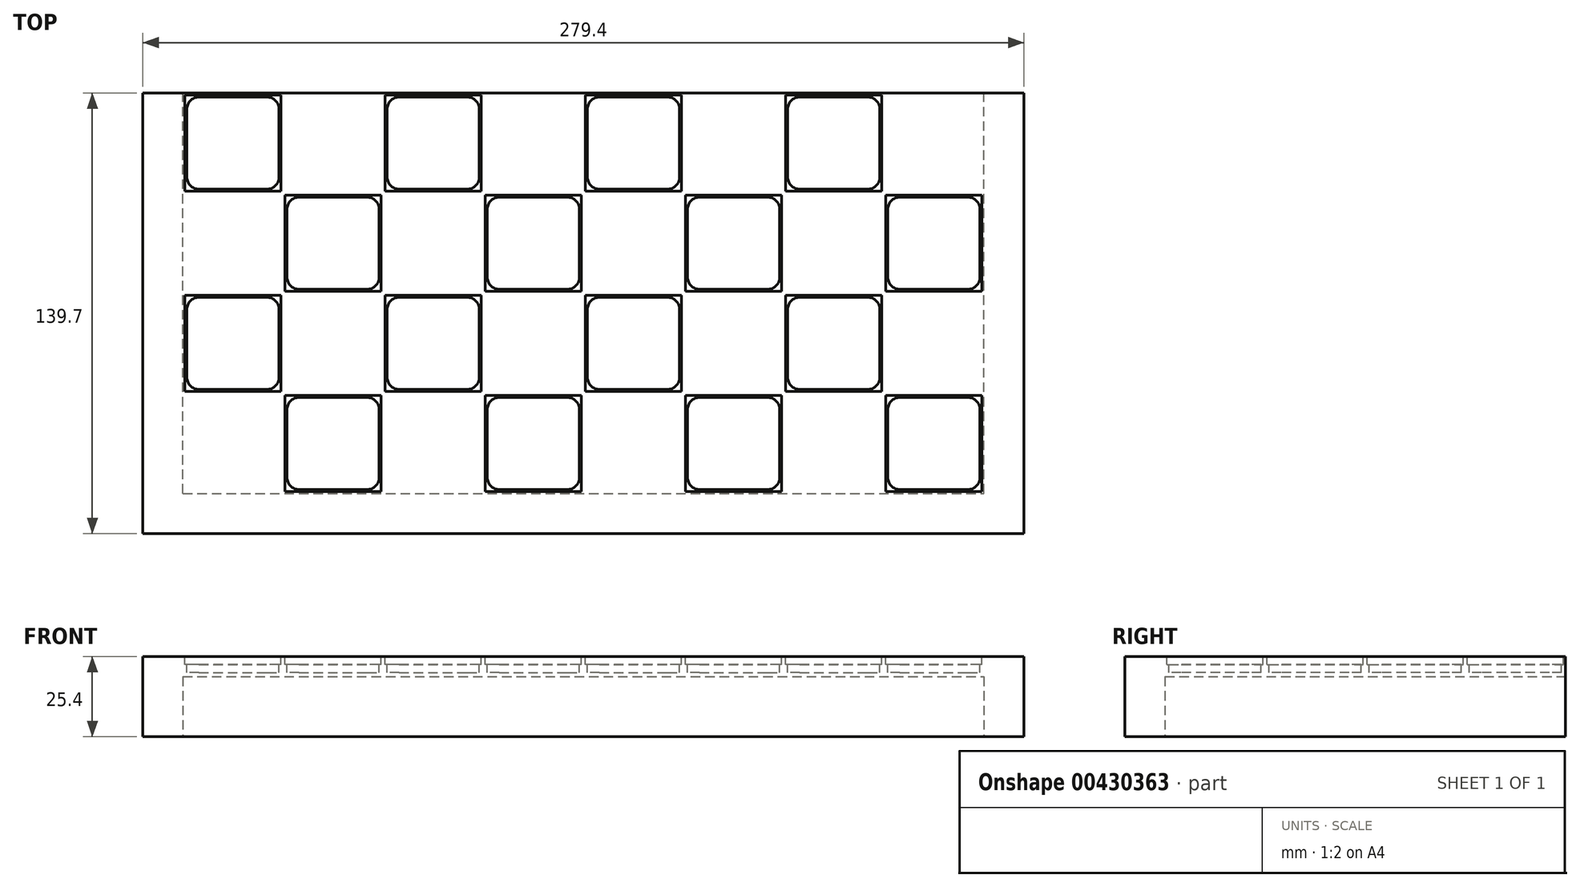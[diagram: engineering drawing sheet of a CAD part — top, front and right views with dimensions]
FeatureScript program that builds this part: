
annotation { "Feature Type Name" : "Feature", "Feature Type Description" : "" }
export const myFeature = defineFeature(function(context is Context, id is Id, definition is map)
    precondition{}
    {
        {
            var Q0;
            Q0=qCreatedBy(makeId("Front.planeOp"),FACE);
            var sketch = newSketch(context, id + "F0", { "sketchPlane" : qUnion([Q0])});
            skLineSegment(sketch, "E0.bottom", {"start": v(-139.7, 12.7) * mm, "end": v(139.7, 12.7) * mm});
            skLineSegment(sketch, "E0.top", {"start": v(-139.7, -12.7) * mm, "end": v(139.7, -12.7) * mm});
            skLineSegment(sketch, "E0.left", {"start": v(-139.7, 12.7) * mm, "end": v(-139.7, -12.7) * mm});
            skLineSegment(sketch, "E0.right", {"start": v(139.7, 12.7) * mm, "end": v(139.7, -12.7) * mm});
            skPoint(sketch, "E0.middle", {"position": v(0, 0) * mm});
            skSolve(sketch);
        }
        {
            var Q0;
            Q0 = qSketchRegion(id + "F0", true);
            extrude(context, id + "F1", {"entities" : qUnion([Q0]), "depth" : 139.7 * mm});
        }
        {
            var Q0;
            Q0=makeQuery(id+"F1.opExtrude","SWEPT_FACE",FACE,{"disambiguationData":[OSD([sQuery(id+"F0.wireOp",EDGE,"E0.bottom")])]});
            var sketch = newSketch(context, id + "F2", { "sketchPlane" : qUnion([Q0])});
            skLineSegment(sketch, "E1", {"start": v(0, 0) * mm, "end": v(0, -127) * mm, "construction": true});
            skPoint(sketch, "E2", {"position": v(-127, 0) * mm});
            skPoint(sketch, "E3", {"position": v(127, 0) * mm});
            skLineSegment(sketch, "E4", {"start": v(-127, 0) * mm, "end": v(-127, -127) * mm, "construction": true});
            skLineSegment(sketch, "E5", {"start": v(127, 0) * mm, "end": v(127, -127) * mm, "construction": true});
            skLineSegment(sketch, "E6", {"start": v(-127, -31.75) * mm, "end": v(127, -31.75) * mm, "construction": true});
            skLineSegment(sketch, "E7", {"start": v(-127, -63.5) * mm, "end": v(127, -63.5) * mm, "construction": true});
            skLineSegment(sketch, "E8", {"start": v(-127, -95.25) * mm, "end": v(127, -95.25) * mm, "construction": true});
            skLineSegment(sketch, "E9", {"start": v(-127, -127) * mm, "end": v(127, -127) * mm, "construction": true});
            skLineSegment(sketch, "E10.1.0.0", {"start": v(-95.25, 0) * mm, "end": v(-95.25, -127) * mm, "construction": true});
            skLineSegment(sketch, "E10.2.0.0", {"start": v(-63.5, 0) * mm, "end": v(-63.5, -127) * mm, "construction": true});
            skLineSegment(sketch, "E10.3.0.0", {"start": v(-31.75, 0) * mm, "end": v(-31.75, -127) * mm, "construction": true});
            skLineSegment(sketch, "E10.4.0.0", {"start": v(0, 0) * mm, "end": v(0, -139.7) * mm, "construction": true});
            skLineSegment(sketch, "E10.5.0.0", {"start": v(31.75, 0) * mm, "end": v(31.75, -127) * mm, "construction": true});
            skLineSegment(sketch, "E10.6.0.0", {"start": v(63.5, 0) * mm, "end": v(63.5, -127) * mm, "construction": true});
            skLineSegment(sketch, "E10.7.0.0", {"start": v(95.25, 0) * mm, "end": v(95.25, -127) * mm, "construction": true});
            skLineSegment(sketch, "E10.direction1", {"start": v(-127, -139.7) * mm, "end": v(-95.25, -139.7) * mm, "construction": true});
            skPoint(sketch, "E11.orphan", {"position": v(-63.5, -139.7) * mm});
            skPoint(sketch, "E12.orphan", {"position": v(-31.75, -139.7) * mm});
            skPoint(sketch, "E13.orphan", {"position": v(0, -139.7) * mm});
            skPoint(sketch, "E14.orphan", {"position": v(31.75, -139.7) * mm});
            skPoint(sketch, "E15.orphan", {"position": v(63.5, -139.7) * mm});
            skPoint(sketch, "E16.orphan", {"position": v(95.25, -139.7) * mm});
            skLineSegment(sketch, "E17", {"start": v(-127, -31.75) * mm, "end": v(-95.25, 0) * mm, "construction": true});
            skLineSegment(sketch, "E18", {"start": v(-127, 0) * mm, "end": v(-95.25, -31.75) * mm, "construction": true});
            skPoint(sketch, "E19", {"position": v(-111.12, -15.88) * mm});
            skLineSegment(sketch, "E20.bottom", {"start": v(-121.92, -1.27) * mm, "end": v(-100.33, -1.27) * mm});
            skLineSegment(sketch, "E20.top", {"start": v(-121.92, -30.48) * mm, "end": v(-100.33, -30.48) * mm});
            skLineSegment(sketch, "E20.left", {"start": v(-125.73, -5.08) * mm, "end": v(-125.73, -26.67) * mm});
            skLineSegment(sketch, "E20.right", {"start": v(-96.52, -5.08) * mm, "end": v(-96.52, -26.67) * mm});
            skPoint(sketch, "E21.visualSharp", {"position": v(-125.73, -1.27) * mm});
            skArc(sketch, "E21.filletArc", {"start": v(-121.92, -1.27) * mm, "mid": v(-124.61, -2.39) * mm, "end": v(-125.73, -5.08) * mm});
            skPoint(sketch, "E22.visualSharp", {"position": v(-96.52, -1.27) * mm});
            skArc(sketch, "E22.filletArc", {"start": v(-96.52, -5.08) * mm, "mid": v(-97.64, -2.39) * mm, "end": v(-100.33, -1.27) * mm});
            skPoint(sketch, "E23.visualSharp", {"position": v(-96.52, -30.48) * mm});
            skArc(sketch, "E23.filletArc", {"start": v(-100.33, -30.48) * mm, "mid": v(-97.64, -29.36) * mm, "end": v(-96.52, -26.67) * mm});
            skPoint(sketch, "E24.visualSharp", {"position": v(-125.73, -30.48) * mm});
            skArc(sketch, "E24.filletArc", {"start": v(-125.73, -26.67) * mm, "mid": v(-124.61, -29.36) * mm, "end": v(-121.92, -30.48) * mm});
            skLineSegment(sketch, "E25.0.1.0", {"start": v(-125.73, -36.83) * mm, "end": v(-125.73, -58.42) * mm});
            skArc(sketch, "E25.0.1.1", {"start": v(-121.92, -33.02) * mm, "mid": v(-124.61, -34.14) * mm, "end": v(-125.73, -36.83) * mm});
            skLineSegment(sketch, "E25.0.1.2", {"start": v(-121.92, -33.02) * mm, "end": v(-100.33, -33.02) * mm});
            skArc(sketch, "E25.0.1.3", {"start": v(-96.52, -36.83) * mm, "mid": v(-97.64, -34.14) * mm, "end": v(-100.33, -33.02) * mm});
            skLineSegment(sketch, "E25.0.1.4", {"start": v(-96.52, -36.83) * mm, "end": v(-96.52, -58.42) * mm});
            skArc(sketch, "E25.0.1.5", {"start": v(-100.33, -62.23) * mm, "mid": v(-97.64, -61.11) * mm, "end": v(-96.52, -58.42) * mm});
            skLineSegment(sketch, "E25.0.1.6", {"start": v(-121.92, -62.23) * mm, "end": v(-100.33, -62.23) * mm});
            skArc(sketch, "E25.0.1.7", {"start": v(-125.73, -58.42) * mm, "mid": v(-124.61, -61.11) * mm, "end": v(-121.92, -62.23) * mm});
            skLineSegment(sketch, "E25.0.2.0", {"start": v(-125.73, -68.58) * mm, "end": v(-125.73, -90.17) * mm});
            skArc(sketch, "E25.0.2.1", {"start": v(-121.92, -64.77) * mm, "mid": v(-124.61, -65.89) * mm, "end": v(-125.73, -68.58) * mm});
            skLineSegment(sketch, "E25.0.2.2", {"start": v(-121.92, -64.77) * mm, "end": v(-100.33, -64.77) * mm});
            skArc(sketch, "E25.0.2.3", {"start": v(-96.52, -68.58) * mm, "mid": v(-97.64, -65.89) * mm, "end": v(-100.33, -64.77) * mm});
            skLineSegment(sketch, "E25.0.2.4", {"start": v(-96.52, -68.58) * mm, "end": v(-96.52, -90.17) * mm});
            skArc(sketch, "E25.0.2.5", {"start": v(-100.33, -93.98) * mm, "mid": v(-97.64, -92.86) * mm, "end": v(-96.52, -90.17) * mm});
            skLineSegment(sketch, "E25.0.2.6", {"start": v(-121.92, -93.98) * mm, "end": v(-100.33, -93.98) * mm});
            skArc(sketch, "E25.0.2.7", {"start": v(-125.73, -90.17) * mm, "mid": v(-124.61, -92.86) * mm, "end": v(-121.92, -93.98) * mm});
            skLineSegment(sketch, "E25.0.3.0", {"start": v(-125.73, -100.33) * mm, "end": v(-125.73, -121.92) * mm});
            skArc(sketch, "E25.0.3.1", {"start": v(-121.92, -96.52) * mm, "mid": v(-124.61, -97.64) * mm, "end": v(-125.73, -100.33) * mm});
            skLineSegment(sketch, "E25.0.3.2", {"start": v(-121.92, -96.52) * mm, "end": v(-100.33, -96.52) * mm});
            skArc(sketch, "E25.0.3.3", {"start": v(-96.52, -100.33) * mm, "mid": v(-97.64, -97.64) * mm, "end": v(-100.33, -96.52) * mm});
            skLineSegment(sketch, "E25.0.3.4", {"start": v(-96.52, -100.33) * mm, "end": v(-96.52, -121.92) * mm});
            skArc(sketch, "E25.0.3.5", {"start": v(-100.33, -125.73) * mm, "mid": v(-97.64, -124.61) * mm, "end": v(-96.52, -121.92) * mm});
            skLineSegment(sketch, "E25.0.3.6", {"start": v(-121.92, -125.73) * mm, "end": v(-100.33, -125.73) * mm});
            skArc(sketch, "E25.0.3.7", {"start": v(-125.73, -121.92) * mm, "mid": v(-124.61, -124.61) * mm, "end": v(-121.92, -125.73) * mm});
            skLineSegment(sketch, "E25.1.0.0", {"start": v(-93.98, -5.08) * mm, "end": v(-93.98, -26.67) * mm});
            skArc(sketch, "E25.1.0.1", {"start": v(-90.17, -1.27) * mm, "mid": v(-92.86, -2.39) * mm, "end": v(-93.98, -5.08) * mm});
            skLineSegment(sketch, "E25.1.0.2", {"start": v(-90.17, -1.27) * mm, "end": v(-68.58, -1.27) * mm});
            skArc(sketch, "E25.1.0.3", {"start": v(-64.77, -5.08) * mm, "mid": v(-65.89, -2.39) * mm, "end": v(-68.58, -1.27) * mm});
            skLineSegment(sketch, "E25.1.0.4", {"start": v(-64.77, -5.08) * mm, "end": v(-64.77, -26.67) * mm});
            skArc(sketch, "E25.1.0.5", {"start": v(-68.58, -30.48) * mm, "mid": v(-65.89, -29.36) * mm, "end": v(-64.77, -26.67) * mm});
            skLineSegment(sketch, "E25.1.0.6", {"start": v(-90.17, -30.48) * mm, "end": v(-68.58, -30.48) * mm});
            skArc(sketch, "E25.1.0.7", {"start": v(-93.98, -26.67) * mm, "mid": v(-92.86, -29.36) * mm, "end": v(-90.17, -30.48) * mm});
            skLineSegment(sketch, "E25.1.1.0", {"start": v(-93.98, -36.83) * mm, "end": v(-93.98, -58.42) * mm});
            skArc(sketch, "E25.1.1.1", {"start": v(-90.17, -33.02) * mm, "mid": v(-92.86, -34.14) * mm, "end": v(-93.98, -36.83) * mm});
            skLineSegment(sketch, "E25.1.1.2", {"start": v(-90.17, -33.02) * mm, "end": v(-68.58, -33.02) * mm});
            skArc(sketch, "E25.1.1.3", {"start": v(-64.77, -36.83) * mm, "mid": v(-65.89, -34.14) * mm, "end": v(-68.58, -33.02) * mm});
            skLineSegment(sketch, "E25.1.1.4", {"start": v(-64.77, -36.83) * mm, "end": v(-64.77, -58.42) * mm});
            skArc(sketch, "E25.1.1.5", {"start": v(-68.58, -62.23) * mm, "mid": v(-65.89, -61.11) * mm, "end": v(-64.77, -58.42) * mm});
            skLineSegment(sketch, "E25.1.1.6", {"start": v(-90.17, -62.23) * mm, "end": v(-68.58, -62.23) * mm});
            skArc(sketch, "E25.1.1.7", {"start": v(-93.98, -58.42) * mm, "mid": v(-92.86, -61.11) * mm, "end": v(-90.17, -62.23) * mm});
            skLineSegment(sketch, "E25.1.2.0", {"start": v(-93.98, -68.58) * mm, "end": v(-93.98, -90.17) * mm});
            skArc(sketch, "E25.1.2.1", {"start": v(-90.17, -64.77) * mm, "mid": v(-92.86, -65.89) * mm, "end": v(-93.98, -68.58) * mm});
            skLineSegment(sketch, "E25.1.2.2", {"start": v(-90.17, -64.77) * mm, "end": v(-68.58, -64.77) * mm});
            skArc(sketch, "E25.1.2.3", {"start": v(-64.77, -68.58) * mm, "mid": v(-65.89, -65.89) * mm, "end": v(-68.58, -64.77) * mm});
            skLineSegment(sketch, "E25.1.2.4", {"start": v(-64.77, -68.58) * mm, "end": v(-64.77, -90.17) * mm});
            skArc(sketch, "E25.1.2.5", {"start": v(-68.58, -93.98) * mm, "mid": v(-65.89, -92.86) * mm, "end": v(-64.77, -90.17) * mm});
            skLineSegment(sketch, "E25.1.2.6", {"start": v(-90.17, -93.98) * mm, "end": v(-68.58, -93.98) * mm});
            skArc(sketch, "E25.1.2.7", {"start": v(-93.98, -90.17) * mm, "mid": v(-92.86, -92.86) * mm, "end": v(-90.17, -93.98) * mm});
            skLineSegment(sketch, "E25.1.3.0", {"start": v(-93.98, -100.33) * mm, "end": v(-93.98, -121.92) * mm});
            skArc(sketch, "E25.1.3.1", {"start": v(-90.17, -96.52) * mm, "mid": v(-92.86, -97.64) * mm, "end": v(-93.98, -100.33) * mm});
            skLineSegment(sketch, "E25.1.3.2", {"start": v(-90.17, -96.52) * mm, "end": v(-68.58, -96.52) * mm});
            skArc(sketch, "E25.1.3.3", {"start": v(-64.77, -100.33) * mm, "mid": v(-65.89, -97.64) * mm, "end": v(-68.58, -96.52) * mm});
            skLineSegment(sketch, "E25.1.3.4", {"start": v(-64.77, -100.33) * mm, "end": v(-64.77, -121.92) * mm});
            skArc(sketch, "E25.1.3.5", {"start": v(-68.58, -125.73) * mm, "mid": v(-65.89, -124.61) * mm, "end": v(-64.77, -121.92) * mm});
            skLineSegment(sketch, "E25.1.3.6", {"start": v(-90.17, -125.73) * mm, "end": v(-68.58, -125.73) * mm});
            skArc(sketch, "E25.1.3.7", {"start": v(-93.98, -121.92) * mm, "mid": v(-92.86, -124.61) * mm, "end": v(-90.17, -125.73) * mm});
            skLineSegment(sketch, "E25.2.0.0", {"start": v(-62.23, -5.08) * mm, "end": v(-62.23, -26.67) * mm});
            skArc(sketch, "E25.2.0.1", {"start": v(-58.42, -1.27) * mm, "mid": v(-61.11, -2.39) * mm, "end": v(-62.23, -5.08) * mm});
            skLineSegment(sketch, "E25.2.0.2", {"start": v(-58.42, -1.27) * mm, "end": v(-36.83, -1.27) * mm});
            skArc(sketch, "E25.2.0.3", {"start": v(-33.02, -5.08) * mm, "mid": v(-34.14, -2.39) * mm, "end": v(-36.83, -1.27) * mm});
            skLineSegment(sketch, "E25.2.0.4", {"start": v(-33.02, -5.08) * mm, "end": v(-33.02, -26.67) * mm});
            skArc(sketch, "E25.2.0.5", {"start": v(-36.83, -30.48) * mm, "mid": v(-34.14, -29.36) * mm, "end": v(-33.02, -26.67) * mm});
            skLineSegment(sketch, "E25.2.0.6", {"start": v(-58.42, -30.48) * mm, "end": v(-36.83, -30.48) * mm});
            skArc(sketch, "E25.2.0.7", {"start": v(-62.23, -26.67) * mm, "mid": v(-61.11, -29.36) * mm, "end": v(-58.42, -30.48) * mm});
            skLineSegment(sketch, "E25.2.1.0", {"start": v(-62.23, -36.83) * mm, "end": v(-62.23, -58.42) * mm});
            skArc(sketch, "E25.2.1.1", {"start": v(-58.42, -33.02) * mm, "mid": v(-61.11, -34.14) * mm, "end": v(-62.23, -36.83) * mm});
            skLineSegment(sketch, "E25.2.1.2", {"start": v(-58.42, -33.02) * mm, "end": v(-36.83, -33.02) * mm});
            skArc(sketch, "E25.2.1.3", {"start": v(-33.02, -36.83) * mm, "mid": v(-34.14, -34.14) * mm, "end": v(-36.83, -33.02) * mm});
            skLineSegment(sketch, "E25.2.1.4", {"start": v(-33.02, -36.83) * mm, "end": v(-33.02, -58.42) * mm});
            skArc(sketch, "E25.2.1.5", {"start": v(-36.83, -62.23) * mm, "mid": v(-34.14, -61.11) * mm, "end": v(-33.02, -58.42) * mm});
            skLineSegment(sketch, "E25.2.1.6", {"start": v(-58.42, -62.23) * mm, "end": v(-36.83, -62.23) * mm});
            skArc(sketch, "E25.2.1.7", {"start": v(-62.23, -58.42) * mm, "mid": v(-61.11, -61.11) * mm, "end": v(-58.42, -62.23) * mm});
            skLineSegment(sketch, "E25.2.2.0", {"start": v(-62.23, -68.58) * mm, "end": v(-62.23, -90.17) * mm});
            skArc(sketch, "E25.2.2.1", {"start": v(-58.42, -64.77) * mm, "mid": v(-61.11, -65.89) * mm, "end": v(-62.23, -68.58) * mm});
            skLineSegment(sketch, "E25.2.2.2", {"start": v(-58.42, -64.77) * mm, "end": v(-36.83, -64.77) * mm});
            skArc(sketch, "E25.2.2.3", {"start": v(-33.02, -68.58) * mm, "mid": v(-34.14, -65.89) * mm, "end": v(-36.83, -64.77) * mm});
            skLineSegment(sketch, "E25.2.2.4", {"start": v(-33.02, -68.58) * mm, "end": v(-33.02, -90.17) * mm});
            skArc(sketch, "E25.2.2.5", {"start": v(-36.83, -93.98) * mm, "mid": v(-34.14, -92.86) * mm, "end": v(-33.02, -90.17) * mm});
            skLineSegment(sketch, "E25.2.2.6", {"start": v(-58.42, -93.98) * mm, "end": v(-36.83, -93.98) * mm});
            skArc(sketch, "E25.2.2.7", {"start": v(-62.23, -90.17) * mm, "mid": v(-61.11, -92.86) * mm, "end": v(-58.42, -93.98) * mm});
            skLineSegment(sketch, "E25.2.3.0", {"start": v(-62.23, -100.33) * mm, "end": v(-62.23, -121.92) * mm});
            skArc(sketch, "E25.2.3.1", {"start": v(-58.42, -96.52) * mm, "mid": v(-61.11, -97.64) * mm, "end": v(-62.23, -100.33) * mm});
            skLineSegment(sketch, "E25.2.3.2", {"start": v(-58.42, -96.52) * mm, "end": v(-36.83, -96.52) * mm});
            skArc(sketch, "E25.2.3.3", {"start": v(-33.02, -100.33) * mm, "mid": v(-34.14, -97.64) * mm, "end": v(-36.83, -96.52) * mm});
            skLineSegment(sketch, "E25.2.3.4", {"start": v(-33.02, -100.33) * mm, "end": v(-33.02, -121.92) * mm});
            skArc(sketch, "E25.2.3.5", {"start": v(-36.83, -125.73) * mm, "mid": v(-34.14, -124.61) * mm, "end": v(-33.02, -121.92) * mm});
            skLineSegment(sketch, "E25.2.3.6", {"start": v(-58.42, -125.73) * mm, "end": v(-36.83, -125.73) * mm});
            skArc(sketch, "E25.2.3.7", {"start": v(-62.23, -121.92) * mm, "mid": v(-61.11, -124.61) * mm, "end": v(-58.42, -125.73) * mm});
            skLineSegment(sketch, "E25.3.0.0", {"start": v(-30.48, -5.08) * mm, "end": v(-30.48, -26.67) * mm});
            skArc(sketch, "E25.3.0.1", {"start": v(-26.67, -1.27) * mm, "mid": v(-29.36, -2.39) * mm, "end": v(-30.48, -5.08) * mm});
            skLineSegment(sketch, "E25.3.0.2", {"start": v(-26.67, -1.27) * mm, "end": v(-5.08, -1.27) * mm});
            skArc(sketch, "E25.3.0.3", {"start": v(-1.27, -5.08) * mm, "mid": v(-2.39, -2.39) * mm, "end": v(-5.08, -1.27) * mm});
            skLineSegment(sketch, "E25.3.0.4", {"start": v(-1.27, -5.08) * mm, "end": v(-1.27, -26.67) * mm});
            skArc(sketch, "E25.3.0.5", {"start": v(-5.08, -30.48) * mm, "mid": v(-2.39, -29.36) * mm, "end": v(-1.27, -26.67) * mm});
            skLineSegment(sketch, "E25.3.0.6", {"start": v(-26.67, -30.48) * mm, "end": v(-5.08, -30.48) * mm});
            skArc(sketch, "E25.3.0.7", {"start": v(-30.48, -26.67) * mm, "mid": v(-29.36, -29.36) * mm, "end": v(-26.67, -30.48) * mm});
            skLineSegment(sketch, "E25.3.1.0", {"start": v(-30.48, -36.83) * mm, "end": v(-30.48, -58.42) * mm});
            skArc(sketch, "E25.3.1.1", {"start": v(-26.67, -33.02) * mm, "mid": v(-29.36, -34.14) * mm, "end": v(-30.48, -36.83) * mm});
            skLineSegment(sketch, "E25.3.1.2", {"start": v(-26.67, -33.02) * mm, "end": v(-5.08, -33.02) * mm});
            skArc(sketch, "E25.3.1.3", {"start": v(-1.27, -36.83) * mm, "mid": v(-2.39, -34.14) * mm, "end": v(-5.08, -33.02) * mm});
            skLineSegment(sketch, "E25.3.1.4", {"start": v(-1.27, -36.83) * mm, "end": v(-1.27, -58.42) * mm});
            skArc(sketch, "E25.3.1.5", {"start": v(-5.08, -62.23) * mm, "mid": v(-2.39, -61.11) * mm, "end": v(-1.27, -58.42) * mm});
            skLineSegment(sketch, "E25.3.1.6", {"start": v(-26.67, -62.23) * mm, "end": v(-5.08, -62.23) * mm});
            skArc(sketch, "E25.3.1.7", {"start": v(-30.48, -58.42) * mm, "mid": v(-29.36, -61.11) * mm, "end": v(-26.67, -62.23) * mm});
            skLineSegment(sketch, "E25.3.2.0", {"start": v(-30.48, -68.58) * mm, "end": v(-30.48, -90.17) * mm});
            skArc(sketch, "E25.3.2.1", {"start": v(-26.67, -64.77) * mm, "mid": v(-29.36, -65.89) * mm, "end": v(-30.48, -68.58) * mm});
            skLineSegment(sketch, "E25.3.2.2", {"start": v(-26.67, -64.77) * mm, "end": v(-5.08, -64.77) * mm});
            skArc(sketch, "E25.3.2.3", {"start": v(-1.27, -68.58) * mm, "mid": v(-2.39, -65.89) * mm, "end": v(-5.08, -64.77) * mm});
            skLineSegment(sketch, "E25.3.2.4", {"start": v(-1.27, -68.58) * mm, "end": v(-1.27, -90.17) * mm});
            skArc(sketch, "E25.3.2.5", {"start": v(-5.08, -93.98) * mm, "mid": v(-2.39, -92.86) * mm, "end": v(-1.27, -90.17) * mm});
            skLineSegment(sketch, "E25.3.2.6", {"start": v(-26.67, -93.98) * mm, "end": v(-5.08, -93.98) * mm});
            skArc(sketch, "E25.3.2.7", {"start": v(-30.48, -90.17) * mm, "mid": v(-29.36, -92.86) * mm, "end": v(-26.67, -93.98) * mm});
            skLineSegment(sketch, "E25.3.3.0", {"start": v(-30.48, -100.33) * mm, "end": v(-30.48, -121.92) * mm});
            skArc(sketch, "E25.3.3.1", {"start": v(-26.67, -96.52) * mm, "mid": v(-29.36, -97.64) * mm, "end": v(-30.48, -100.33) * mm});
            skLineSegment(sketch, "E25.3.3.2", {"start": v(-26.67, -96.52) * mm, "end": v(-5.08, -96.52) * mm});
            skArc(sketch, "E25.3.3.3", {"start": v(-1.27, -100.33) * mm, "mid": v(-2.39, -97.64) * mm, "end": v(-5.08, -96.52) * mm});
            skLineSegment(sketch, "E25.3.3.4", {"start": v(-1.27, -100.33) * mm, "end": v(-1.27, -121.92) * mm});
            skArc(sketch, "E25.3.3.5", {"start": v(-5.08, -125.73) * mm, "mid": v(-2.39, -124.61) * mm, "end": v(-1.27, -121.92) * mm});
            skLineSegment(sketch, "E25.3.3.6", {"start": v(-26.67, -125.73) * mm, "end": v(-5.08, -125.73) * mm});
            skArc(sketch, "E25.3.3.7", {"start": v(-30.48, -121.92) * mm, "mid": v(-29.36, -124.61) * mm, "end": v(-26.67, -125.73) * mm});
            skLineSegment(sketch, "E25.4.0.0", {"start": v(1.27, -5.08) * mm, "end": v(1.27, -26.67) * mm});
            skArc(sketch, "E25.4.0.1", {"start": v(5.08, -1.27) * mm, "mid": v(2.39, -2.39) * mm, "end": v(1.27, -5.08) * mm});
            skLineSegment(sketch, "E25.4.0.2", {"start": v(5.08, -1.27) * mm, "end": v(26.67, -1.27) * mm});
            skArc(sketch, "E25.4.0.3", {"start": v(30.48, -5.08) * mm, "mid": v(29.36, -2.39) * mm, "end": v(26.67, -1.27) * mm});
            skLineSegment(sketch, "E25.4.0.4", {"start": v(30.48, -5.08) * mm, "end": v(30.48, -26.67) * mm});
            skArc(sketch, "E25.4.0.5", {"start": v(26.67, -30.48) * mm, "mid": v(29.36, -29.36) * mm, "end": v(30.48, -26.67) * mm});
            skLineSegment(sketch, "E25.4.0.6", {"start": v(5.08, -30.48) * mm, "end": v(26.67, -30.48) * mm});
            skArc(sketch, "E25.4.0.7", {"start": v(1.27, -26.67) * mm, "mid": v(2.39, -29.36) * mm, "end": v(5.08, -30.48) * mm});
            skLineSegment(sketch, "E25.4.1.0", {"start": v(1.27, -36.83) * mm, "end": v(1.27, -58.42) * mm});
            skArc(sketch, "E25.4.1.1", {"start": v(5.08, -33.02) * mm, "mid": v(2.39, -34.14) * mm, "end": v(1.27, -36.83) * mm});
            skLineSegment(sketch, "E25.4.1.2", {"start": v(5.08, -33.02) * mm, "end": v(26.67, -33.02) * mm});
            skArc(sketch, "E25.4.1.3", {"start": v(30.48, -36.83) * mm, "mid": v(29.36, -34.14) * mm, "end": v(26.67, -33.02) * mm});
            skLineSegment(sketch, "E25.4.1.4", {"start": v(30.48, -36.83) * mm, "end": v(30.48, -58.42) * mm});
            skArc(sketch, "E25.4.1.5", {"start": v(26.67, -62.23) * mm, "mid": v(29.36, -61.11) * mm, "end": v(30.48, -58.42) * mm});
            skLineSegment(sketch, "E25.4.1.6", {"start": v(5.08, -62.23) * mm, "end": v(26.67, -62.23) * mm});
            skArc(sketch, "E25.4.1.7", {"start": v(1.27, -58.42) * mm, "mid": v(2.39, -61.11) * mm, "end": v(5.08, -62.23) * mm});
            skLineSegment(sketch, "E25.4.2.0", {"start": v(1.27, -68.58) * mm, "end": v(1.27, -90.17) * mm});
            skArc(sketch, "E25.4.2.1", {"start": v(5.08, -64.77) * mm, "mid": v(2.39, -65.89) * mm, "end": v(1.27, -68.58) * mm});
            skLineSegment(sketch, "E25.4.2.2", {"start": v(5.08, -64.77) * mm, "end": v(26.67, -64.77) * mm});
            skArc(sketch, "E25.4.2.3", {"start": v(30.48, -68.58) * mm, "mid": v(29.36, -65.89) * mm, "end": v(26.67, -64.77) * mm});
            skLineSegment(sketch, "E25.4.2.4", {"start": v(30.48, -68.58) * mm, "end": v(30.48, -90.17) * mm});
            skArc(sketch, "E25.4.2.5", {"start": v(26.67, -93.98) * mm, "mid": v(29.36, -92.86) * mm, "end": v(30.48, -90.17) * mm});
            skLineSegment(sketch, "E25.4.2.6", {"start": v(5.08, -93.98) * mm, "end": v(26.67, -93.98) * mm});
            skArc(sketch, "E25.4.2.7", {"start": v(1.27, -90.17) * mm, "mid": v(2.39, -92.86) * mm, "end": v(5.08, -93.98) * mm});
            skLineSegment(sketch, "E25.4.3.0", {"start": v(1.27, -100.33) * mm, "end": v(1.27, -121.92) * mm});
            skArc(sketch, "E25.4.3.1", {"start": v(5.08, -96.52) * mm, "mid": v(2.39, -97.64) * mm, "end": v(1.27, -100.33) * mm});
            skLineSegment(sketch, "E25.4.3.2", {"start": v(5.08, -96.52) * mm, "end": v(26.67, -96.52) * mm});
            skArc(sketch, "E25.4.3.3", {"start": v(30.48, -100.33) * mm, "mid": v(29.36, -97.64) * mm, "end": v(26.67, -96.52) * mm});
            skLineSegment(sketch, "E25.4.3.4", {"start": v(30.48, -100.33) * mm, "end": v(30.48, -121.92) * mm});
            skArc(sketch, "E25.4.3.5", {"start": v(26.67, -125.73) * mm, "mid": v(29.36, -124.61) * mm, "end": v(30.48, -121.92) * mm});
            skLineSegment(sketch, "E25.4.3.6", {"start": v(5.08, -125.73) * mm, "end": v(26.67, -125.73) * mm});
            skArc(sketch, "E25.4.3.7", {"start": v(1.27, -121.92) * mm, "mid": v(2.39, -124.61) * mm, "end": v(5.08, -125.73) * mm});
            skLineSegment(sketch, "E25.5.0.0", {"start": v(33.02, -5.08) * mm, "end": v(33.02, -26.67) * mm});
            skArc(sketch, "E25.5.0.1", {"start": v(36.83, -1.27) * mm, "mid": v(34.14, -2.39) * mm, "end": v(33.02, -5.08) * mm});
            skLineSegment(sketch, "E25.5.0.2", {"start": v(36.83, -1.27) * mm, "end": v(58.42, -1.27) * mm});
            skArc(sketch, "E25.5.0.3", {"start": v(62.23, -5.08) * mm, "mid": v(61.11, -2.39) * mm, "end": v(58.42, -1.27) * mm});
            skLineSegment(sketch, "E25.5.0.4", {"start": v(62.23, -5.08) * mm, "end": v(62.23, -26.67) * mm});
            skArc(sketch, "E25.5.0.5", {"start": v(58.42, -30.48) * mm, "mid": v(61.11, -29.36) * mm, "end": v(62.23, -26.67) * mm});
            skLineSegment(sketch, "E25.5.0.6", {"start": v(36.83, -30.48) * mm, "end": v(58.42, -30.48) * mm});
            skArc(sketch, "E25.5.0.7", {"start": v(33.02, -26.67) * mm, "mid": v(34.14, -29.36) * mm, "end": v(36.83, -30.48) * mm});
            skLineSegment(sketch, "E25.5.1.0", {"start": v(33.02, -36.83) * mm, "end": v(33.02, -58.42) * mm});
            skArc(sketch, "E25.5.1.1", {"start": v(36.83, -33.02) * mm, "mid": v(34.14, -34.14) * mm, "end": v(33.02, -36.83) * mm});
            skLineSegment(sketch, "E25.5.1.2", {"start": v(36.83, -33.02) * mm, "end": v(58.42, -33.02) * mm});
            skArc(sketch, "E25.5.1.3", {"start": v(62.23, -36.83) * mm, "mid": v(61.11, -34.14) * mm, "end": v(58.42, -33.02) * mm});
            skLineSegment(sketch, "E25.5.1.4", {"start": v(62.23, -36.83) * mm, "end": v(62.23, -58.42) * mm});
            skArc(sketch, "E25.5.1.5", {"start": v(58.42, -62.23) * mm, "mid": v(61.11, -61.11) * mm, "end": v(62.23, -58.42) * mm});
            skLineSegment(sketch, "E25.5.1.6", {"start": v(36.83, -62.23) * mm, "end": v(58.42, -62.23) * mm});
            skArc(sketch, "E25.5.1.7", {"start": v(33.02, -58.42) * mm, "mid": v(34.14, -61.11) * mm, "end": v(36.83, -62.23) * mm});
            skLineSegment(sketch, "E25.5.2.0", {"start": v(33.02, -68.58) * mm, "end": v(33.02, -90.17) * mm});
            skArc(sketch, "E25.5.2.1", {"start": v(36.83, -64.77) * mm, "mid": v(34.14, -65.89) * mm, "end": v(33.02, -68.58) * mm});
            skLineSegment(sketch, "E25.5.2.2", {"start": v(36.83, -64.77) * mm, "end": v(58.42, -64.77) * mm});
            skArc(sketch, "E25.5.2.3", {"start": v(62.23, -68.58) * mm, "mid": v(61.11, -65.89) * mm, "end": v(58.42, -64.77) * mm});
            skLineSegment(sketch, "E25.5.2.4", {"start": v(62.23, -68.58) * mm, "end": v(62.23, -90.17) * mm});
            skArc(sketch, "E25.5.2.5", {"start": v(58.42, -93.98) * mm, "mid": v(61.11, -92.86) * mm, "end": v(62.23, -90.17) * mm});
            skLineSegment(sketch, "E25.5.2.6", {"start": v(36.83, -93.98) * mm, "end": v(58.42, -93.98) * mm});
            skArc(sketch, "E25.5.2.7", {"start": v(33.02, -90.17) * mm, "mid": v(34.14, -92.86) * mm, "end": v(36.83, -93.98) * mm});
            skLineSegment(sketch, "E25.5.3.0", {"start": v(33.02, -100.33) * mm, "end": v(33.02, -121.92) * mm});
            skArc(sketch, "E25.5.3.1", {"start": v(36.83, -96.52) * mm, "mid": v(34.14, -97.64) * mm, "end": v(33.02, -100.33) * mm});
            skLineSegment(sketch, "E25.5.3.2", {"start": v(36.83, -96.52) * mm, "end": v(58.42, -96.52) * mm});
            skArc(sketch, "E25.5.3.3", {"start": v(62.23, -100.33) * mm, "mid": v(61.11, -97.64) * mm, "end": v(58.42, -96.52) * mm});
            skLineSegment(sketch, "E25.5.3.4", {"start": v(62.23, -100.33) * mm, "end": v(62.23, -121.92) * mm});
            skArc(sketch, "E25.5.3.5", {"start": v(58.42, -125.73) * mm, "mid": v(61.11, -124.61) * mm, "end": v(62.23, -121.92) * mm});
            skLineSegment(sketch, "E25.5.3.6", {"start": v(36.83, -125.73) * mm, "end": v(58.42, -125.73) * mm});
            skArc(sketch, "E25.5.3.7", {"start": v(33.02, -121.92) * mm, "mid": v(34.14, -124.61) * mm, "end": v(36.83, -125.73) * mm});
            skLineSegment(sketch, "E25.6.0.0", {"start": v(64.77, -5.08) * mm, "end": v(64.77, -26.67) * mm});
            skArc(sketch, "E25.6.0.1", {"start": v(68.58, -1.27) * mm, "mid": v(65.89, -2.39) * mm, "end": v(64.77, -5.08) * mm});
            skLineSegment(sketch, "E25.6.0.2", {"start": v(68.58, -1.27) * mm, "end": v(90.17, -1.27) * mm});
            skArc(sketch, "E25.6.0.3", {"start": v(93.98, -5.08) * mm, "mid": v(92.86, -2.39) * mm, "end": v(90.17, -1.27) * mm});
            skLineSegment(sketch, "E25.6.0.4", {"start": v(93.98, -5.08) * mm, "end": v(93.98, -26.67) * mm});
            skArc(sketch, "E25.6.0.5", {"start": v(90.17, -30.48) * mm, "mid": v(92.86, -29.36) * mm, "end": v(93.98, -26.67) * mm});
            skLineSegment(sketch, "E25.6.0.6", {"start": v(68.58, -30.48) * mm, "end": v(90.17, -30.48) * mm});
            skArc(sketch, "E25.6.0.7", {"start": v(64.77, -26.67) * mm, "mid": v(65.89, -29.36) * mm, "end": v(68.58, -30.48) * mm});
            skLineSegment(sketch, "E25.6.1.0", {"start": v(64.77, -36.83) * mm, "end": v(64.77, -58.42) * mm});
            skArc(sketch, "E25.6.1.1", {"start": v(68.58, -33.02) * mm, "mid": v(65.89, -34.14) * mm, "end": v(64.77, -36.83) * mm});
            skLineSegment(sketch, "E25.6.1.2", {"start": v(68.58, -33.02) * mm, "end": v(90.17, -33.02) * mm});
            skArc(sketch, "E25.6.1.3", {"start": v(93.98, -36.83) * mm, "mid": v(92.86, -34.14) * mm, "end": v(90.17, -33.02) * mm});
            skLineSegment(sketch, "E25.6.1.4", {"start": v(93.98, -36.83) * mm, "end": v(93.98, -58.42) * mm});
            skArc(sketch, "E25.6.1.5", {"start": v(90.17, -62.23) * mm, "mid": v(92.86, -61.11) * mm, "end": v(93.98, -58.42) * mm});
            skLineSegment(sketch, "E25.6.1.6", {"start": v(68.58, -62.23) * mm, "end": v(90.17, -62.23) * mm});
            skArc(sketch, "E25.6.1.7", {"start": v(64.77, -58.42) * mm, "mid": v(65.89, -61.11) * mm, "end": v(68.58, -62.23) * mm});
            skLineSegment(sketch, "E25.6.2.0", {"start": v(64.77, -68.58) * mm, "end": v(64.77, -90.17) * mm});
            skArc(sketch, "E25.6.2.1", {"start": v(68.58, -64.77) * mm, "mid": v(65.89, -65.89) * mm, "end": v(64.77, -68.58) * mm});
            skLineSegment(sketch, "E25.6.2.2", {"start": v(68.58, -64.77) * mm, "end": v(90.17, -64.77) * mm});
            skArc(sketch, "E25.6.2.3", {"start": v(93.98, -68.58) * mm, "mid": v(92.86, -65.89) * mm, "end": v(90.17, -64.77) * mm});
            skLineSegment(sketch, "E25.6.2.4", {"start": v(93.98, -68.58) * mm, "end": v(93.98, -90.17) * mm});
            skArc(sketch, "E25.6.2.5", {"start": v(90.17, -93.98) * mm, "mid": v(92.86, -92.86) * mm, "end": v(93.98, -90.17) * mm});
            skLineSegment(sketch, "E25.6.2.6", {"start": v(68.58, -93.98) * mm, "end": v(90.17, -93.98) * mm});
            skArc(sketch, "E25.6.2.7", {"start": v(64.77, -90.17) * mm, "mid": v(65.89, -92.86) * mm, "end": v(68.58, -93.98) * mm});
            skLineSegment(sketch, "E25.6.3.0", {"start": v(64.77, -100.33) * mm, "end": v(64.77, -121.92) * mm});
            skArc(sketch, "E25.6.3.1", {"start": v(68.58, -96.52) * mm, "mid": v(65.89, -97.64) * mm, "end": v(64.77, -100.33) * mm});
            skLineSegment(sketch, "E25.6.3.2", {"start": v(68.58, -96.52) * mm, "end": v(90.17, -96.52) * mm});
            skArc(sketch, "E25.6.3.3", {"start": v(93.98, -100.33) * mm, "mid": v(92.86, -97.64) * mm, "end": v(90.17, -96.52) * mm});
            skLineSegment(sketch, "E25.6.3.4", {"start": v(93.98, -100.33) * mm, "end": v(93.98, -121.92) * mm});
            skArc(sketch, "E25.6.3.5", {"start": v(90.17, -125.73) * mm, "mid": v(92.86, -124.61) * mm, "end": v(93.98, -121.92) * mm});
            skLineSegment(sketch, "E25.6.3.6", {"start": v(68.58, -125.73) * mm, "end": v(90.17, -125.73) * mm});
            skArc(sketch, "E25.6.3.7", {"start": v(64.77, -121.92) * mm, "mid": v(65.89, -124.61) * mm, "end": v(68.58, -125.73) * mm});
            skLineSegment(sketch, "E25.7.0.0", {"start": v(96.52, -5.08) * mm, "end": v(96.52, -26.67) * mm});
            skArc(sketch, "E25.7.0.1", {"start": v(100.33, -1.27) * mm, "mid": v(97.64, -2.39) * mm, "end": v(96.52, -5.08) * mm});
            skLineSegment(sketch, "E25.7.0.2", {"start": v(100.33, -1.27) * mm, "end": v(121.92, -1.27) * mm});
            skArc(sketch, "E25.7.0.3", {"start": v(125.73, -5.08) * mm, "mid": v(124.61, -2.39) * mm, "end": v(121.92, -1.27) * mm});
            skLineSegment(sketch, "E25.7.0.4", {"start": v(125.73, -5.08) * mm, "end": v(125.73, -26.67) * mm});
            skArc(sketch, "E25.7.0.5", {"start": v(121.92, -30.48) * mm, "mid": v(124.61, -29.36) * mm, "end": v(125.73, -26.67) * mm});
            skLineSegment(sketch, "E25.7.0.6", {"start": v(100.33, -30.48) * mm, "end": v(121.92, -30.48) * mm});
            skArc(sketch, "E25.7.0.7", {"start": v(96.52, -26.67) * mm, "mid": v(97.64, -29.36) * mm, "end": v(100.33, -30.48) * mm});
            skLineSegment(sketch, "E25.7.1.0", {"start": v(96.52, -36.83) * mm, "end": v(96.52, -58.42) * mm});
            skArc(sketch, "E25.7.1.1", {"start": v(100.33, -33.02) * mm, "mid": v(97.64, -34.14) * mm, "end": v(96.52, -36.83) * mm});
            skLineSegment(sketch, "E25.7.1.2", {"start": v(100.33, -33.02) * mm, "end": v(121.92, -33.02) * mm});
            skArc(sketch, "E25.7.1.3", {"start": v(125.73, -36.83) * mm, "mid": v(124.61, -34.14) * mm, "end": v(121.92, -33.02) * mm});
            skLineSegment(sketch, "E25.7.1.4", {"start": v(125.73, -36.83) * mm, "end": v(125.73, -58.42) * mm});
            skArc(sketch, "E25.7.1.5", {"start": v(121.92, -62.23) * mm, "mid": v(124.61, -61.11) * mm, "end": v(125.73, -58.42) * mm});
            skLineSegment(sketch, "E25.7.1.6", {"start": v(100.33, -62.23) * mm, "end": v(121.92, -62.23) * mm});
            skArc(sketch, "E25.7.1.7", {"start": v(96.52, -58.42) * mm, "mid": v(97.64, -61.11) * mm, "end": v(100.33, -62.23) * mm});
            skLineSegment(sketch, "E25.7.2.0", {"start": v(96.52, -68.58) * mm, "end": v(96.52, -90.17) * mm});
            skArc(sketch, "E25.7.2.1", {"start": v(100.33, -64.77) * mm, "mid": v(97.64, -65.89) * mm, "end": v(96.52, -68.58) * mm});
            skLineSegment(sketch, "E25.7.2.2", {"start": v(100.33, -64.77) * mm, "end": v(121.92, -64.77) * mm});
            skArc(sketch, "E25.7.2.3", {"start": v(125.73, -68.58) * mm, "mid": v(124.61, -65.89) * mm, "end": v(121.92, -64.77) * mm});
            skLineSegment(sketch, "E25.7.2.4", {"start": v(125.73, -68.58) * mm, "end": v(125.73, -90.17) * mm});
            skArc(sketch, "E25.7.2.5", {"start": v(121.92, -93.98) * mm, "mid": v(124.61, -92.86) * mm, "end": v(125.73, -90.17) * mm});
            skLineSegment(sketch, "E25.7.2.6", {"start": v(100.33, -93.98) * mm, "end": v(121.92, -93.98) * mm});
            skArc(sketch, "E25.7.2.7", {"start": v(96.52, -90.17) * mm, "mid": v(97.64, -92.86) * mm, "end": v(100.33, -93.98) * mm});
            skLineSegment(sketch, "E25.7.3.0", {"start": v(96.52, -100.33) * mm, "end": v(96.52, -121.92) * mm});
            skArc(sketch, "E25.7.3.1", {"start": v(100.33, -96.52) * mm, "mid": v(97.64, -97.64) * mm, "end": v(96.52, -100.33) * mm});
            skLineSegment(sketch, "E25.7.3.2", {"start": v(100.33, -96.52) * mm, "end": v(121.92, -96.52) * mm});
            skArc(sketch, "E25.7.3.3", {"start": v(125.73, -100.33) * mm, "mid": v(124.61, -97.64) * mm, "end": v(121.92, -96.52) * mm});
            skLineSegment(sketch, "E25.7.3.4", {"start": v(125.73, -100.33) * mm, "end": v(125.73, -121.92) * mm});
            skArc(sketch, "E25.7.3.5", {"start": v(121.92, -125.73) * mm, "mid": v(124.61, -124.61) * mm, "end": v(125.73, -121.92) * mm});
            skLineSegment(sketch, "E25.7.3.6", {"start": v(100.33, -125.73) * mm, "end": v(121.92, -125.73) * mm});
            skArc(sketch, "E25.7.3.7", {"start": v(96.52, -121.92) * mm, "mid": v(97.64, -124.61) * mm, "end": v(100.33, -125.73) * mm});
            skLineSegment(sketch, "E25.direction1", {"start": v(-121.92, -30.48) * mm, "end": v(-90.17, -30.48) * mm, "construction": true});
            skLineSegment(sketch, "E25.direction2", {"start": v(-121.92, -30.48) * mm, "end": v(-121.92, -62.23) * mm, "construction": true});
            skSolve(sketch);
        }
        {
            var Q0;
            Q0=makeQuery(id+"F2.imprint","IMPRINT",FACE,{"disambiguationData":[TD([[makeQuery(id+"F2.imprint","IMPRINT",EDGE,{"derivedFrom":sQuery(id+"F2.wireOp",EDGE,"E20.bottom")}),-1.0]])]});
            var Q1;
            Q1=makeQuery(id+"F2.imprint","IMPRINT",FACE,{"disambiguationData":[TD([[makeQuery(id+"F2.imprint","IMPRINT",EDGE,{"derivedFrom":sQuery(id+"F2.wireOp",EDGE,"E25.0.2.0")}),1.0]])]});
            var Q2;
            Q2=makeQuery(id+"F2.imprint","IMPRINT",FACE,{"disambiguationData":[TD([[makeQuery(id+"F2.imprint","IMPRINT",EDGE,{"derivedFrom":sQuery(id+"F2.wireOp",EDGE,"E25.2.0.0")}),1.0]])]});
            var Q3;
            Q3=makeQuery(id+"F2.imprint","IMPRINT",FACE,{"disambiguationData":[TD([[makeQuery(id+"F2.imprint","IMPRINT",EDGE,{"derivedFrom":sQuery(id+"F2.wireOp",EDGE,"E25.1.1.0")}),1.0]])]});
            var Q4;
            Q4=makeQuery(id+"F2.imprint","IMPRINT",FACE,{"disambiguationData":[TD([[makeQuery(id+"F2.imprint","IMPRINT",EDGE,{"derivedFrom":sQuery(id+"F2.wireOp",EDGE,"E25.2.2.0")}),1.0]])]});
            var Q5;
            Q5=makeQuery(id+"F2.imprint","IMPRINT",FACE,{"disambiguationData":[TD([[makeQuery(id+"F2.imprint","IMPRINT",EDGE,{"derivedFrom":sQuery(id+"F2.wireOp",EDGE,"E25.1.3.0")}),1.0]])]});
            var Q6;
            Q6=makeQuery(id+"F2.imprint","IMPRINT",FACE,{"disambiguationData":[TD([[makeQuery(id+"F2.imprint","IMPRINT",EDGE,{"derivedFrom":sQuery(id+"F2.wireOp",EDGE,"E25.3.3.0")}),1.0]])]});
            var Q7;
            Q7=makeQuery(id+"F2.imprint","IMPRINT",FACE,{"disambiguationData":[TD([[makeQuery(id+"F2.imprint","IMPRINT",EDGE,{"derivedFrom":sQuery(id+"F2.wireOp",EDGE,"E25.4.2.0")}),1.0]])]});
            var Q8;
            Q8=makeQuery(id+"F2.imprint","IMPRINT",FACE,{"disambiguationData":[TD([[makeQuery(id+"F2.imprint","IMPRINT",EDGE,{"derivedFrom":sQuery(id+"F2.wireOp",EDGE,"E25.3.1.0")}),1.0]])]});
            var Q9;
            Q9=makeQuery(id+"F2.imprint","IMPRINT",FACE,{"disambiguationData":[TD([[makeQuery(id+"F2.imprint","IMPRINT",EDGE,{"derivedFrom":sQuery(id+"F2.wireOp",EDGE,"E25.4.0.0")}),1.0]])]});
            var Q10;
            Q10=makeQuery(id+"F2.imprint","IMPRINT",FACE,{"disambiguationData":[TD([[makeQuery(id+"F2.imprint","IMPRINT",EDGE,{"derivedFrom":sQuery(id+"F2.wireOp",EDGE,"E25.5.1.0")}),1.0]])]});
            var Q11;
            Q11=makeQuery(id+"F2.imprint","IMPRINT",FACE,{"disambiguationData":[TD([[makeQuery(id+"F2.imprint","IMPRINT",EDGE,{"derivedFrom":sQuery(id+"F2.wireOp",EDGE,"E25.6.2.0")}),1.0]])]});
            var Q12;
            Q12=makeQuery(id+"F2.imprint","IMPRINT",FACE,{"disambiguationData":[TD([[makeQuery(id+"F2.imprint","IMPRINT",EDGE,{"derivedFrom":sQuery(id+"F2.wireOp",EDGE,"E25.5.3.0")}),1.0]])]});
            var Q13;
            Q13=makeQuery(id+"F2.imprint","IMPRINT",FACE,{"disambiguationData":[TD([[makeQuery(id+"F2.imprint","IMPRINT",EDGE,{"derivedFrom":sQuery(id+"F2.wireOp",EDGE,"E25.7.3.0")}),1.0]])]});
            var Q14;
            Q14=makeQuery(id+"F2.imprint","IMPRINT",FACE,{"disambiguationData":[TD([[makeQuery(id+"F2.imprint","IMPRINT",EDGE,{"derivedFrom":sQuery(id+"F2.wireOp",EDGE,"E25.7.1.0")}),1.0]])]});
            var Q15;
            Q15=makeQuery(id+"F2.imprint","IMPRINT",FACE,{"disambiguationData":[TD([[makeQuery(id+"F2.imprint","IMPRINT",EDGE,{"derivedFrom":sQuery(id+"F2.wireOp",EDGE,"E25.6.0.0")}),1.0]])]});
            extrude(context, id + "F3", {"entities" : qUnion([Q0, Q1, Q2, Q3, Q4, Q5, Q6, Q7, Q8, Q9, Q10, Q11, Q12, Q13, Q14, Q15]), "operationType" : NewBodyOperationType.REMOVE, "oppositeDirection" : true, "depth" : 5.08 * mm});
        }
        {
            var Q0;
            Q0=makeQuery(id+"F1.opExtrude","SWEPT_FACE",FACE,{"disambiguationData":[OSD([sQuery(id+"F0.wireOp",EDGE,"E0.top")])]});
            var sketch = newSketch(context, id + "F4", { "sketchPlane" : qUnion([Q0])});
            skLineSegment(sketch, "E26", {"start": v(-139.7, 0) * mm, "end": v(139.7, 139.7) * mm, "construction": true});
            skLineSegment(sketch, "E27", {"start": v(-139.7, 139.7) * mm, "end": v(139.7, 0) * mm, "construction": true});
            skPoint(sketch, "E28", {"position": v(0, 69.85) * mm});
            skLineSegment(sketch, "E29.bottom", {"start": v(-127, 127) * mm, "end": v(127, 127) * mm});
            skLineSegment(sketch, "E29.top", {"start": v(-127, 12.7) * mm, "end": v(127, 12.7) * mm, "construction": true});
            skLineSegment(sketch, "E29.left", {"start": v(-127, 127) * mm, "end": v(-127, 12.7) * mm});
            skLineSegment(sketch, "E29.right", {"start": v(127, 127) * mm, "end": v(127, 12.7) * mm});
            skLineSegment(sketch, "E30", {"start": v(-127, 12.7) * mm, "end": v(-127, 0) * mm});
            skLineSegment(sketch, "E31", {"start": v(127, 12.7) * mm, "end": v(127, 0) * mm});
            skSolve(sketch);
        }
        {
            var Q0;
            Q0=makeQuery(id+"F4.imprint","IMPRINT",FACE,{"disambiguationData":[TD([[makeQuery(id+"F4.imprint","IMPRINT",EDGE,{"derivedFrom":sQuery(id+"F4.wireOp",EDGE,"E29.bottom")}),-1.0]])]});
            var Q1;
            Q1=makeQuery(id+"F3.boolean.opBoolean","COPY",FACE,{"derivedFrom":makeQuery(id+"F3.opExtrude","CAP_FACE",FACE,{"disambiguationData":[OSD([sQuery(id+"F2.wireOp",EDGE,"E25.4.2.0"),sQuery(id+"F2.wireOp",EDGE,"E25.4.2.1"),sQuery(id+"F2.wireOp",EDGE,"E25.4.2.2"),sQuery(id+"F2.wireOp",EDGE,"E25.4.2.3"),sQuery(id+"F2.wireOp",EDGE,"E25.4.2.4"),sQuery(id+"F2.wireOp",EDGE,"E25.4.2.5"),sQuery(id+"F2.wireOp",EDGE,"E25.4.2.6"),sQuery(id+"F2.wireOp",EDGE,"E25.4.2.7")])],"isStart":false})});
            extrude(context, id + "F5", {"entities" : qUnion([Q0]), "operationType" : NewBodyOperationType.REMOVE, "oppositeDirection" : true, "endBoundEntityFace" : qUnion([Q1]), "depth" : 19.05 * mm});
        }
        {
            var Q0;
            Q0=makeQuery(id+"F1.opExtrude","SWEPT_FACE",FACE,{"disambiguationData":[OSD([sQuery(id+"F0.wireOp",EDGE,"E0.bottom")])]});
            var sketch = newSketch(context, id + "F6", { "sketchPlane" : qUnion([Q0])});
            skLineSegment(sketch, "E32", {"start": v(111.12, -125.73) * mm, "end": v(111.12, -96.52) * mm, "construction": true});
            skLineSegment(sketch, "E33", {"start": v(125.73, -111.12) * mm, "end": v(96.52, -111.12) * mm, "construction": true});
            skLineSegment(sketch, "E34.bottom", {"start": v(126.36, -126.36) * mm, "end": v(95.88, -126.36) * mm});
            skLineSegment(sketch, "E34.top", {"start": v(126.36, -95.88) * mm, "end": v(95.88, -95.88) * mm});
            skLineSegment(sketch, "E34.left", {"start": v(126.36, -126.36) * mm, "end": v(126.36, -95.88) * mm});
            skLineSegment(sketch, "E34.right", {"start": v(95.88, -126.36) * mm, "end": v(95.88, -95.88) * mm});
            skPoint(sketch, "E34.middle", {"position": v(111.12, -111.12) * mm});
            skLineSegment(sketch, "E35.0.1.0", {"start": v(126.36, -94.61) * mm, "end": v(95.88, -94.61) * mm});
            skLineSegment(sketch, "E35.0.1.1", {"start": v(126.36, -94.61) * mm, "end": v(126.36, -64.13) * mm});
            skLineSegment(sketch, "E35.0.1.2", {"start": v(95.88, -94.61) * mm, "end": v(95.88, -64.13) * mm});
            skLineSegment(sketch, "E35.0.1.3", {"start": v(126.36, -64.13) * mm, "end": v(95.88, -64.13) * mm});
            skLineSegment(sketch, "E35.0.2.0", {"start": v(126.36, -62.86) * mm, "end": v(95.88, -62.86) * mm});
            skLineSegment(sketch, "E35.0.2.1", {"start": v(126.36, -62.86) * mm, "end": v(126.36, -32.38) * mm});
            skLineSegment(sketch, "E35.0.2.2", {"start": v(95.88, -62.86) * mm, "end": v(95.88, -32.38) * mm});
            skLineSegment(sketch, "E35.0.2.3", {"start": v(126.36, -32.38) * mm, "end": v(95.88, -32.38) * mm});
            skLineSegment(sketch, "E35.0.3.0", {"start": v(126.36, -31.11) * mm, "end": v(95.88, -31.11) * mm});
            skLineSegment(sketch, "E35.0.3.1", {"start": v(126.36, -31.11) * mm, "end": v(126.36, -0.63) * mm});
            skLineSegment(sketch, "E35.0.3.2", {"start": v(95.88, -31.11) * mm, "end": v(95.88, -0.63) * mm});
            skLineSegment(sketch, "E35.0.3.3", {"start": v(126.36, -0.63) * mm, "end": v(95.88, -0.63) * mm});
            skLineSegment(sketch, "E35.1.0.0", {"start": v(94.61, -126.36) * mm, "end": v(64.13, -126.36) * mm});
            skLineSegment(sketch, "E35.1.0.1", {"start": v(94.61, -126.36) * mm, "end": v(94.61, -95.88) * mm});
            skLineSegment(sketch, "E35.1.0.2", {"start": v(64.13, -126.36) * mm, "end": v(64.13, -95.88) * mm});
            skLineSegment(sketch, "E35.1.0.3", {"start": v(94.61, -95.88) * mm, "end": v(64.13, -95.88) * mm});
            skLineSegment(sketch, "E35.1.1.0", {"start": v(94.61, -94.61) * mm, "end": v(64.13, -94.61) * mm});
            skLineSegment(sketch, "E35.1.1.1", {"start": v(94.61, -94.61) * mm, "end": v(94.61, -64.13) * mm});
            skLineSegment(sketch, "E35.1.1.2", {"start": v(64.13, -94.61) * mm, "end": v(64.13, -64.13) * mm});
            skLineSegment(sketch, "E35.1.1.3", {"start": v(94.61, -64.13) * mm, "end": v(64.13, -64.13) * mm});
            skLineSegment(sketch, "E35.1.2.0", {"start": v(94.61, -62.86) * mm, "end": v(64.13, -62.86) * mm});
            skLineSegment(sketch, "E35.1.2.1", {"start": v(94.61, -62.86) * mm, "end": v(94.61, -32.38) * mm});
            skLineSegment(sketch, "E35.1.2.2", {"start": v(64.13, -62.86) * mm, "end": v(64.13, -32.38) * mm});
            skLineSegment(sketch, "E35.1.2.3", {"start": v(94.61, -32.38) * mm, "end": v(64.13, -32.38) * mm});
            skLineSegment(sketch, "E35.1.3.0", {"start": v(94.61, -31.11) * mm, "end": v(64.13, -31.11) * mm});
            skLineSegment(sketch, "E35.1.3.1", {"start": v(94.61, -31.11) * mm, "end": v(94.61, -0.63) * mm});
            skLineSegment(sketch, "E35.1.3.2", {"start": v(64.13, -31.11) * mm, "end": v(64.13, -0.63) * mm});
            skLineSegment(sketch, "E35.1.3.3", {"start": v(94.61, -0.63) * mm, "end": v(64.13, -0.63) * mm});
            skLineSegment(sketch, "E35.2.0.0", {"start": v(62.86, -126.36) * mm, "end": v(32.38, -126.36) * mm});
            skLineSegment(sketch, "E35.2.0.1", {"start": v(62.86, -126.36) * mm, "end": v(62.86, -95.88) * mm});
            skLineSegment(sketch, "E35.2.0.2", {"start": v(32.38, -126.36) * mm, "end": v(32.38, -95.88) * mm});
            skLineSegment(sketch, "E35.2.0.3", {"start": v(62.86, -95.88) * mm, "end": v(32.38, -95.88) * mm});
            skLineSegment(sketch, "E35.2.1.0", {"start": v(62.86, -94.61) * mm, "end": v(32.38, -94.61) * mm});
            skLineSegment(sketch, "E35.2.1.1", {"start": v(62.86, -94.61) * mm, "end": v(62.86, -64.13) * mm});
            skLineSegment(sketch, "E35.2.1.2", {"start": v(32.38, -94.61) * mm, "end": v(32.38, -64.13) * mm});
            skLineSegment(sketch, "E35.2.1.3", {"start": v(62.86, -64.13) * mm, "end": v(32.38, -64.13) * mm});
            skLineSegment(sketch, "E35.2.2.0", {"start": v(62.86, -62.86) * mm, "end": v(32.38, -62.86) * mm});
            skLineSegment(sketch, "E35.2.2.1", {"start": v(62.86, -62.86) * mm, "end": v(62.86, -32.38) * mm});
            skLineSegment(sketch, "E35.2.2.2", {"start": v(32.38, -62.86) * mm, "end": v(32.38, -32.38) * mm});
            skLineSegment(sketch, "E35.2.2.3", {"start": v(62.86, -32.38) * mm, "end": v(32.38, -32.38) * mm});
            skLineSegment(sketch, "E35.2.3.0", {"start": v(62.86, -31.11) * mm, "end": v(32.38, -31.11) * mm});
            skLineSegment(sketch, "E35.2.3.1", {"start": v(62.86, -31.11) * mm, "end": v(62.86, -0.63) * mm});
            skLineSegment(sketch, "E35.2.3.2", {"start": v(32.38, -31.11) * mm, "end": v(32.38, -0.63) * mm});
            skLineSegment(sketch, "E35.2.3.3", {"start": v(62.86, -0.63) * mm, "end": v(32.38, -0.63) * mm});
            skLineSegment(sketch, "E35.3.0.0", {"start": v(31.11, -126.36) * mm, "end": v(0.63, -126.36) * mm});
            skLineSegment(sketch, "E35.3.0.1", {"start": v(31.11, -126.36) * mm, "end": v(31.11, -95.88) * mm});
            skLineSegment(sketch, "E35.3.0.2", {"start": v(0.63, -126.36) * mm, "end": v(0.63, -95.88) * mm});
            skLineSegment(sketch, "E35.3.0.3", {"start": v(31.11, -95.88) * mm, "end": v(0.63, -95.88) * mm});
            skLineSegment(sketch, "E35.3.1.0", {"start": v(31.11, -94.61) * mm, "end": v(0.63, -94.61) * mm});
            skLineSegment(sketch, "E35.3.1.1", {"start": v(31.11, -94.61) * mm, "end": v(31.11, -64.13) * mm});
            skLineSegment(sketch, "E35.3.1.2", {"start": v(0.63, -94.61) * mm, "end": v(0.63, -64.13) * mm});
            skLineSegment(sketch, "E35.3.1.3", {"start": v(31.11, -64.13) * mm, "end": v(0.63, -64.13) * mm});
            skLineSegment(sketch, "E35.3.2.0", {"start": v(31.11, -62.86) * mm, "end": v(0.63, -62.86) * mm});
            skLineSegment(sketch, "E35.3.2.1", {"start": v(31.11, -62.86) * mm, "end": v(31.11, -32.38) * mm});
            skLineSegment(sketch, "E35.3.2.2", {"start": v(0.63, -62.86) * mm, "end": v(0.63, -32.38) * mm});
            skLineSegment(sketch, "E35.3.2.3", {"start": v(31.11, -32.38) * mm, "end": v(0.63, -32.38) * mm});
            skLineSegment(sketch, "E35.3.3.0", {"start": v(31.11, -31.11) * mm, "end": v(0.63, -31.11) * mm});
            skLineSegment(sketch, "E35.3.3.1", {"start": v(31.11, -31.11) * mm, "end": v(31.11, -0.63) * mm});
            skLineSegment(sketch, "E35.3.3.2", {"start": v(0.63, -31.11) * mm, "end": v(0.63, -0.63) * mm});
            skLineSegment(sketch, "E35.3.3.3", {"start": v(31.11, -0.63) * mm, "end": v(0.63, -0.63) * mm});
            skLineSegment(sketch, "E35.4.0.0", {"start": v(-0.64, -126.36) * mm, "end": v(-31.12, -126.36) * mm});
            skLineSegment(sketch, "E35.4.0.1", {"start": v(-0.64, -126.36) * mm, "end": v(-0.64, -95.88) * mm});
            skLineSegment(sketch, "E35.4.0.2", {"start": v(-31.12, -126.36) * mm, "end": v(-31.12, -95.88) * mm});
            skLineSegment(sketch, "E35.4.0.3", {"start": v(-0.64, -95.88) * mm, "end": v(-31.12, -95.88) * mm});
            skLineSegment(sketch, "E35.4.1.0", {"start": v(-0.64, -94.61) * mm, "end": v(-31.12, -94.61) * mm});
            skLineSegment(sketch, "E35.4.1.1", {"start": v(-0.64, -94.61) * mm, "end": v(-0.64, -64.13) * mm});
            skLineSegment(sketch, "E35.4.1.2", {"start": v(-31.12, -94.61) * mm, "end": v(-31.12, -64.13) * mm});
            skLineSegment(sketch, "E35.4.1.3", {"start": v(-0.64, -64.13) * mm, "end": v(-31.12, -64.13) * mm});
            skLineSegment(sketch, "E35.4.2.0", {"start": v(-0.64, -62.86) * mm, "end": v(-31.12, -62.86) * mm});
            skLineSegment(sketch, "E35.4.2.1", {"start": v(-0.64, -62.86) * mm, "end": v(-0.64, -32.38) * mm});
            skLineSegment(sketch, "E35.4.2.2", {"start": v(-31.12, -62.86) * mm, "end": v(-31.12, -32.38) * mm});
            skLineSegment(sketch, "E35.4.2.3", {"start": v(-0.64, -32.38) * mm, "end": v(-31.12, -32.38) * mm});
            skLineSegment(sketch, "E35.4.3.0", {"start": v(-0.64, -31.11) * mm, "end": v(-31.12, -31.11) * mm});
            skLineSegment(sketch, "E35.4.3.1", {"start": v(-0.64, -31.11) * mm, "end": v(-0.64, -0.63) * mm});
            skLineSegment(sketch, "E35.4.3.2", {"start": v(-31.12, -31.11) * mm, "end": v(-31.12, -0.63) * mm});
            skLineSegment(sketch, "E35.4.3.3", {"start": v(-0.64, -0.63) * mm, "end": v(-31.12, -0.63) * mm});
            skLineSegment(sketch, "E35.5.0.0", {"start": v(-32.39, -126.36) * mm, "end": v(-62.87, -126.36) * mm});
            skLineSegment(sketch, "E35.5.0.1", {"start": v(-32.39, -126.36) * mm, "end": v(-32.39, -95.88) * mm});
            skLineSegment(sketch, "E35.5.0.2", {"start": v(-62.87, -126.36) * mm, "end": v(-62.87, -95.88) * mm});
            skLineSegment(sketch, "E35.5.0.3", {"start": v(-32.39, -95.88) * mm, "end": v(-62.87, -95.88) * mm});
            skLineSegment(sketch, "E35.5.1.0", {"start": v(-32.39, -94.61) * mm, "end": v(-62.87, -94.61) * mm});
            skLineSegment(sketch, "E35.5.1.1", {"start": v(-32.39, -94.61) * mm, "end": v(-32.39, -64.13) * mm});
            skLineSegment(sketch, "E35.5.1.2", {"start": v(-62.87, -94.61) * mm, "end": v(-62.87, -64.13) * mm});
            skLineSegment(sketch, "E35.5.1.3", {"start": v(-32.39, -64.13) * mm, "end": v(-62.87, -64.13) * mm});
            skLineSegment(sketch, "E35.5.2.0", {"start": v(-32.39, -62.86) * mm, "end": v(-62.87, -62.86) * mm});
            skLineSegment(sketch, "E35.5.2.1", {"start": v(-32.39, -62.86) * mm, "end": v(-32.39, -32.38) * mm});
            skLineSegment(sketch, "E35.5.2.2", {"start": v(-62.87, -62.86) * mm, "end": v(-62.87, -32.38) * mm});
            skLineSegment(sketch, "E35.5.2.3", {"start": v(-32.39, -32.38) * mm, "end": v(-62.87, -32.38) * mm});
            skLineSegment(sketch, "E35.5.3.0", {"start": v(-32.39, -31.11) * mm, "end": v(-62.87, -31.11) * mm});
            skLineSegment(sketch, "E35.5.3.1", {"start": v(-32.39, -31.11) * mm, "end": v(-32.39, -0.63) * mm});
            skLineSegment(sketch, "E35.5.3.2", {"start": v(-62.87, -31.11) * mm, "end": v(-62.87, -0.63) * mm});
            skLineSegment(sketch, "E35.5.3.3", {"start": v(-32.39, -0.63) * mm, "end": v(-62.87, -0.63) * mm});
            skLineSegment(sketch, "E35.6.0.0", {"start": v(-64.14, -126.36) * mm, "end": v(-94.62, -126.36) * mm});
            skLineSegment(sketch, "E35.6.0.1", {"start": v(-64.14, -126.36) * mm, "end": v(-64.14, -95.88) * mm});
            skLineSegment(sketch, "E35.6.0.2", {"start": v(-94.62, -126.36) * mm, "end": v(-94.62, -95.88) * mm});
            skLineSegment(sketch, "E35.6.0.3", {"start": v(-64.14, -95.88) * mm, "end": v(-94.62, -95.88) * mm});
            skLineSegment(sketch, "E35.6.1.0", {"start": v(-64.14, -94.61) * mm, "end": v(-94.62, -94.61) * mm});
            skLineSegment(sketch, "E35.6.1.1", {"start": v(-64.14, -94.61) * mm, "end": v(-64.14, -64.13) * mm});
            skLineSegment(sketch, "E35.6.1.2", {"start": v(-94.62, -94.61) * mm, "end": v(-94.62, -64.13) * mm});
            skLineSegment(sketch, "E35.6.1.3", {"start": v(-64.14, -64.13) * mm, "end": v(-94.62, -64.13) * mm});
            skLineSegment(sketch, "E35.6.2.0", {"start": v(-64.14, -62.86) * mm, "end": v(-94.62, -62.86) * mm});
            skLineSegment(sketch, "E35.6.2.1", {"start": v(-64.14, -62.86) * mm, "end": v(-64.14, -32.38) * mm});
            skLineSegment(sketch, "E35.6.2.2", {"start": v(-94.62, -62.86) * mm, "end": v(-94.62, -32.38) * mm});
            skLineSegment(sketch, "E35.6.2.3", {"start": v(-64.14, -32.38) * mm, "end": v(-94.62, -32.38) * mm});
            skLineSegment(sketch, "E35.6.3.0", {"start": v(-64.14, -31.11) * mm, "end": v(-94.62, -31.11) * mm});
            skLineSegment(sketch, "E35.6.3.1", {"start": v(-64.14, -31.11) * mm, "end": v(-64.14, -0.63) * mm});
            skLineSegment(sketch, "E35.6.3.2", {"start": v(-94.62, -31.11) * mm, "end": v(-94.62, -0.63) * mm});
            skLineSegment(sketch, "E35.6.3.3", {"start": v(-64.14, -0.63) * mm, "end": v(-94.62, -0.63) * mm});
            skLineSegment(sketch, "E35.7.0.0", {"start": v(-95.89, -126.36) * mm, "end": v(-126.37, -126.36) * mm});
            skLineSegment(sketch, "E35.7.0.1", {"start": v(-95.89, -126.36) * mm, "end": v(-95.89, -95.88) * mm});
            skLineSegment(sketch, "E35.7.0.2", {"start": v(-126.37, -126.36) * mm, "end": v(-126.37, -95.88) * mm});
            skLineSegment(sketch, "E35.7.0.3", {"start": v(-95.89, -95.88) * mm, "end": v(-126.37, -95.88) * mm});
            skLineSegment(sketch, "E35.7.1.0", {"start": v(-95.89, -94.61) * mm, "end": v(-126.37, -94.61) * mm});
            skLineSegment(sketch, "E35.7.1.1", {"start": v(-95.89, -94.61) * mm, "end": v(-95.89, -64.13) * mm});
            skLineSegment(sketch, "E35.7.1.2", {"start": v(-126.37, -94.61) * mm, "end": v(-126.37, -64.13) * mm});
            skLineSegment(sketch, "E35.7.1.3", {"start": v(-95.89, -64.13) * mm, "end": v(-126.37, -64.13) * mm});
            skLineSegment(sketch, "E35.7.2.0", {"start": v(-95.89, -62.86) * mm, "end": v(-126.37, -62.86) * mm});
            skLineSegment(sketch, "E35.7.2.1", {"start": v(-95.89, -62.86) * mm, "end": v(-95.89, -32.38) * mm});
            skLineSegment(sketch, "E35.7.2.2", {"start": v(-126.37, -62.86) * mm, "end": v(-126.37, -32.38) * mm});
            skLineSegment(sketch, "E35.7.2.3", {"start": v(-95.89, -32.38) * mm, "end": v(-126.37, -32.38) * mm});
            skLineSegment(sketch, "E35.7.3.0", {"start": v(-95.89, -31.11) * mm, "end": v(-126.37, -31.11) * mm});
            skLineSegment(sketch, "E35.7.3.1", {"start": v(-95.89, -31.11) * mm, "end": v(-95.89, -0.63) * mm});
            skLineSegment(sketch, "E35.7.3.2", {"start": v(-126.37, -31.11) * mm, "end": v(-126.37, -0.63) * mm});
            skLineSegment(sketch, "E35.7.3.3", {"start": v(-95.89, -0.63) * mm, "end": v(-126.37, -0.63) * mm});
            skLineSegment(sketch, "E35.direction1", {"start": v(95.88, -126.36) * mm, "end": v(64.13, -126.36) * mm, "construction": true});
            skLineSegment(sketch, "E35.direction2", {"start": v(95.88, -126.36) * mm, "end": v(95.88, -94.61) * mm, "construction": true});
            skSolve(sketch);
        }
        {
            var Q0;
            Q0=makeQuery(id+"F6.imprint","IMPRINT",FACE,{"disambiguationData":[TD([[makeQuery(id+"F6.imprint","IMPRINT",EDGE,{"derivedFrom":sQuery(id+"F6.wireOp",EDGE,"E34.bottom")}),-1.0]])]});
            var Q1;
            Q1=makeQuery(id+"F6.imprint","IMPRINT",FACE,{"disambiguationData":[TD([[makeQuery(id+"F6.imprint","IMPRINT",EDGE,{"derivedFrom":sQuery(id+"F6.wireOp",EDGE,"E35.2.0.0")}),-1.0]])]});
            var Q2;
            Q2=makeQuery(id+"F6.imprint","IMPRINT",FACE,{"disambiguationData":[TD([[makeQuery(id+"F6.imprint","IMPRINT",EDGE,{"derivedFrom":sQuery(id+"F6.wireOp",EDGE,"E35.0.2.0")}),-1.0]])]});
            var Q3;
            Q3=makeQuery(id+"F6.imprint","IMPRINT",FACE,{"disambiguationData":[TD([[makeQuery(id+"F6.imprint","IMPRINT",EDGE,{"derivedFrom":sQuery(id+"F6.wireOp",EDGE,"E35.1.1.0")}),-1.0]])]});
            var Q4;
            Q4=makeQuery(id+"F6.imprint","IMPRINT",FACE,{"disambiguationData":[TD([[makeQuery(id+"F6.imprint","IMPRINT",EDGE,{"derivedFrom":sQuery(id+"F6.wireOp",EDGE,"E35.1.3.0")}),-1.0]])]});
            var Q5;
            Q5=makeQuery(id+"F6.imprint","IMPRINT",FACE,{"disambiguationData":[TD([[makeQuery(id+"F6.imprint","IMPRINT",EDGE,{"derivedFrom":sQuery(id+"F6.wireOp",EDGE,"E35.2.2.0")}),-1.0]])]});
            var Q6;
            Q6=makeQuery(id+"F6.imprint","IMPRINT",FACE,{"disambiguationData":[TD([[makeQuery(id+"F6.imprint","IMPRINT",EDGE,{"derivedFrom":sQuery(id+"F6.wireOp",EDGE,"E35.3.3.0")}),-1.0]])]});
            var Q7;
            Q7=makeQuery(id+"F6.imprint","IMPRINT",FACE,{"disambiguationData":[TD([[makeQuery(id+"F6.imprint","IMPRINT",EDGE,{"derivedFrom":sQuery(id+"F6.wireOp",EDGE,"E35.3.1.0")}),-1.0]])]});
            var Q8;
            Q8=makeQuery(id+"F6.imprint","IMPRINT",FACE,{"disambiguationData":[TD([[makeQuery(id+"F6.imprint","IMPRINT",EDGE,{"derivedFrom":sQuery(id+"F6.wireOp",EDGE,"E35.4.0.0")}),-1.0]])]});
            var Q9;
            Q9=makeQuery(id+"F6.imprint","IMPRINT",FACE,{"disambiguationData":[TD([[makeQuery(id+"F6.imprint","IMPRINT",EDGE,{"derivedFrom":sQuery(id+"F6.wireOp",EDGE,"E35.4.2.0")}),-1.0]])]});
            var Q10;
            Q10=makeQuery(id+"F6.imprint","IMPRINT",FACE,{"disambiguationData":[TD([[makeQuery(id+"F6.imprint","IMPRINT",EDGE,{"derivedFrom":sQuery(id+"F6.wireOp",EDGE,"E35.5.3.0")}),-1.0]])]});
            var Q11;
            Q11=makeQuery(id+"F6.imprint","IMPRINT",FACE,{"disambiguationData":[TD([[makeQuery(id+"F6.imprint","IMPRINT",EDGE,{"derivedFrom":sQuery(id+"F6.wireOp",EDGE,"E35.5.1.0")}),-1.0]])]});
            var Q12;
            Q12=makeQuery(id+"F6.imprint","IMPRINT",FACE,{"disambiguationData":[TD([[makeQuery(id+"F6.imprint","IMPRINT",EDGE,{"derivedFrom":sQuery(id+"F6.wireOp",EDGE,"E35.6.0.0")}),-1.0]])]});
            var Q13;
            Q13=makeQuery(id+"F6.imprint","IMPRINT",FACE,{"disambiguationData":[TD([[makeQuery(id+"F6.imprint","IMPRINT",EDGE,{"derivedFrom":sQuery(id+"F6.wireOp",EDGE,"E35.6.2.0")}),-1.0]])]});
            var Q14;
            Q14=makeQuery(id+"F6.imprint","IMPRINT",FACE,{"disambiguationData":[TD([[makeQuery(id+"F6.imprint","IMPRINT",EDGE,{"derivedFrom":sQuery(id+"F6.wireOp",EDGE,"E35.7.1.0")}),-1.0]])]});
            var Q15;
            Q15=makeQuery(id+"F6.imprint","IMPRINT",FACE,{"disambiguationData":[TD([[makeQuery(id+"F6.imprint","IMPRINT",EDGE,{"derivedFrom":sQuery(id+"F6.wireOp",EDGE,"E35.7.3.0")}),-1.0]])]});
            extrude(context, id + "F7", {"entities" : qUnion([Q0, Q1, Q2, Q3, Q4, Q5, Q6, Q7, Q8, Q9, Q10, Q11, Q12, Q13, Q14, Q15]), "operationType" : NewBodyOperationType.REMOVE, "oppositeDirection" : true, "depth" : 2.54 * mm});
        }
    });
